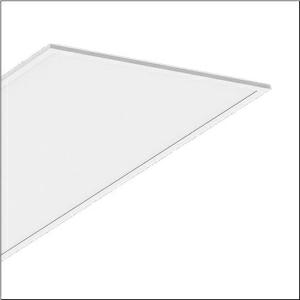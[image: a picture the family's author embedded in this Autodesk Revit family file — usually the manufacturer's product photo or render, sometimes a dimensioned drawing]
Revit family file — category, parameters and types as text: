
# Revit family: apollon_r__21_linear_51mq1awd2m14_9569
name_source: partatom
category: Lighting Fixtures
units: mm (PartAtom-declared; Revit-internal decimal feet)

## family parameters
Cut with Voids When Loaded = No
Host = Face
Light Source = No
Part Type = Normal
Room Calculation Point = No
Round Connector Dimension = Use Diameter
Shared = No

## types (1)
- --- (1 x LED, 7000 lm, 44.5 W, 4000K)
    Apparent Load = 45 VA
    CIE Flux Codes = 60 87 97 100 100
    Color Rendering = 80
    Color Temperature = 4000K
    Default Elevation = 1800 mm
    Description = Apollon® 21 linear, office luminaire, primary optical cover: micro prismatic cover, of PMMA, CAT 2 (L<= 3000cd/m²), light emission: direct distribution, primary light characteristic: symmetric, installation type: lay-in mounting, LED, rated luminous flux: 7.000lm, luminous efficacy: 157lm/W, light colour: 830/840, colour temperature: 3000/4000K, with terminal, 5-pole, mains connection: 220..240V, AC/DC, 0/50..60Hz, rated input power: 44.5W, housing, of aluminium, coated, traffic white (RAL 9016), length: 1.195mm, width: 595mm, height: 30mm, housing upper side, of sheet steel, galvanised, protection rating (complete): IP20, protection rating (lamp compartment, on room side): IP50, insulation class (complete): insulation class II (safety insulation), certification: CE, ENEC, impact resistance: IK03, permissible operating ambient temperature: -20..+45°C, permissible storage temperature: -40..+80°C, packaging unit: 1 piece
    Height = 0 mm  [stored 0 ft]
    Lamp = 1 x LED
    Lamp Light Flux = 7000 lm
    Lamp Power = 44.5 W
    Lamp count = 1
    Length = 1195 mm
    Luminous efficacy = 157 lm/W
    Manufacturer = Siteco
    ModVariant = No
    Model = 51MQ1AWD2M14
    Mounting Place = Ceiling
    Mounting Type = Recessed
    Number of Poles = 1
    OnlyDefault = Yes
    Power Factor = 1
    Product Name = Apollon® 21 linear
    Product group = office luminaire | ceiling recessed
    ProductGroupID = 400
    Protection Class = Protection class II
    Protection Degree = IP 20
    RLX_Detail_Level = 1
    RLX_Emergency_Light_Flux = 0 lm
    RLX_Emergency_Type = 0
    RLX_Emergency_Type_DB = No
    RlxData = <blob elided: 19501 chars, md5=0cfa96f0>
    Socket = socket
    Standby Power = 0 W
    System Light Flux = 7000 lm
    System Power = 45 W
    Type Comments = factory setting
    Type Image = l_1335551.jpg
    URL = http://relux.com
    VarID = @adj_035459
    Voltage = 0 V
    Weight = 0.00 kg
    Width = 595 mm

note: [stored X ft] marks values corroborated as IEEE doubles in the binary element streams (Revit-internal decimal feet)

## geometry (parser evidence)
native form markers: Blend x4, Sweep x12
no freeform markers — native parametric forms only
